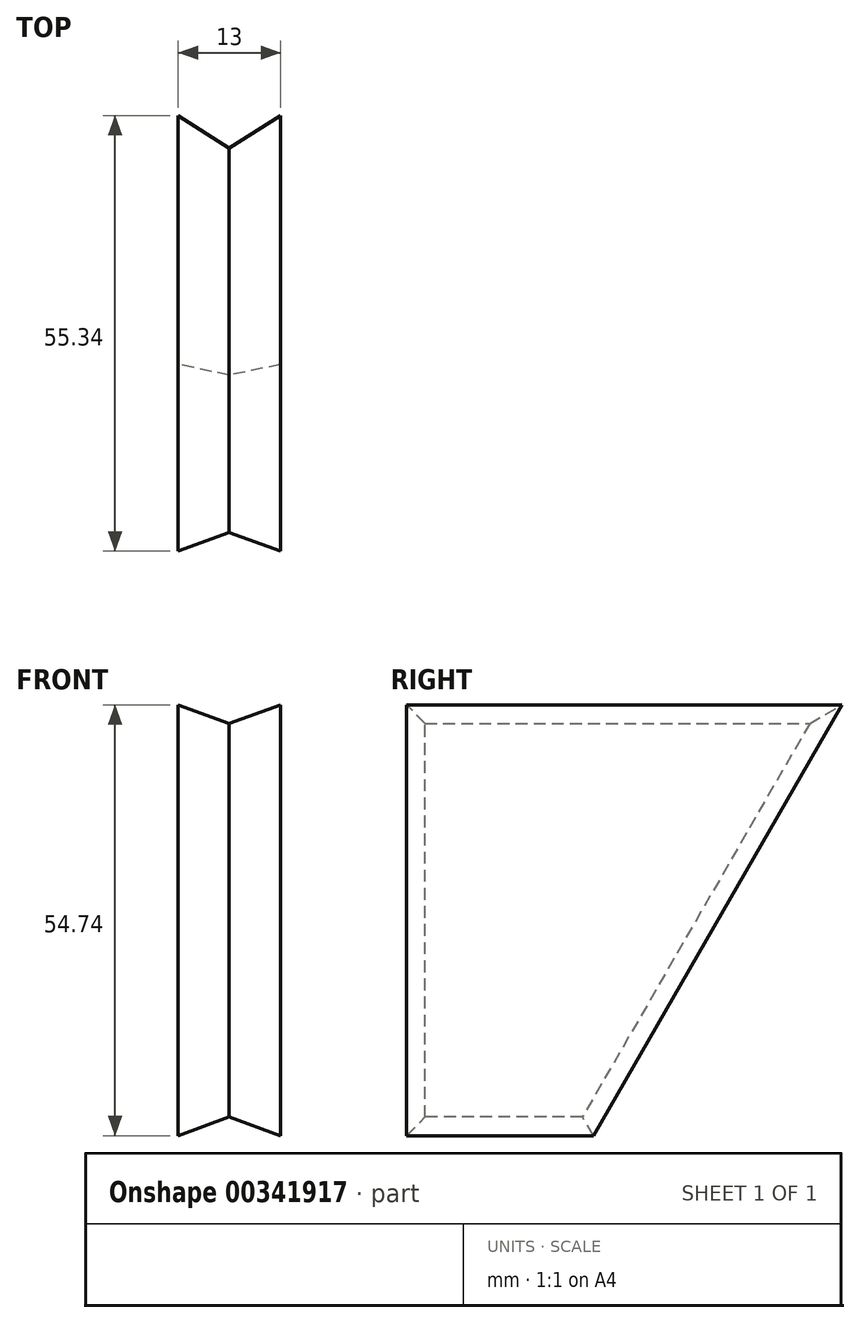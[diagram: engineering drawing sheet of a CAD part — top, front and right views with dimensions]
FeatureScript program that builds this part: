
annotation { "Feature Type Name" : "Feature", "Feature Type Description" : "" }
export const myFeature = defineFeature(function(context is Context, id is Id, definition is map)
    precondition{}
    {
        {
            var Q0;
            Q0=qCreatedBy(makeId("Right.planeOp"),FACE);
            var sketch = newSketch(context, id + "F0", { "sketchPlane" : qUnion([Q0])});
            skLineSegment(sketch, "E0.bottom", {"start": v(20, -50) * mm, "end": v(0, -50) * mm});
            skLineSegment(sketch, "E0.top", {"start": v(48.87, 0) * mm, "end": v(0, 0) * mm});
            skLineSegment(sketch, "E0.right", {"start": v(0, -50) * mm, "end": v(0, 0) * mm});
            skLineSegment(sketch, "E1", {"start": v(48.87, 0) * mm, "end": v(20, -50) * mm});
            skSolve(sketch);
        }
        {
            var Q0;
            Q0=makeQuery(id+"F0.imprint","IMPRINT",FACE,{"disambiguationData":[TD([[makeQuery(id+"F0.imprint","IMPRINT",EDGE,{"derivedFrom":sQuery(id+"F0.wireOp",EDGE,"E0.bottom")}),-1.0]])]});
            extrude(context, id + "F1", {"entities" : qUnion([Q0]), "depth" : 13 * mm, "hasDraft" : true, "draftAngle" : 20 * degree, "symmetric" : true});
        }
    });
